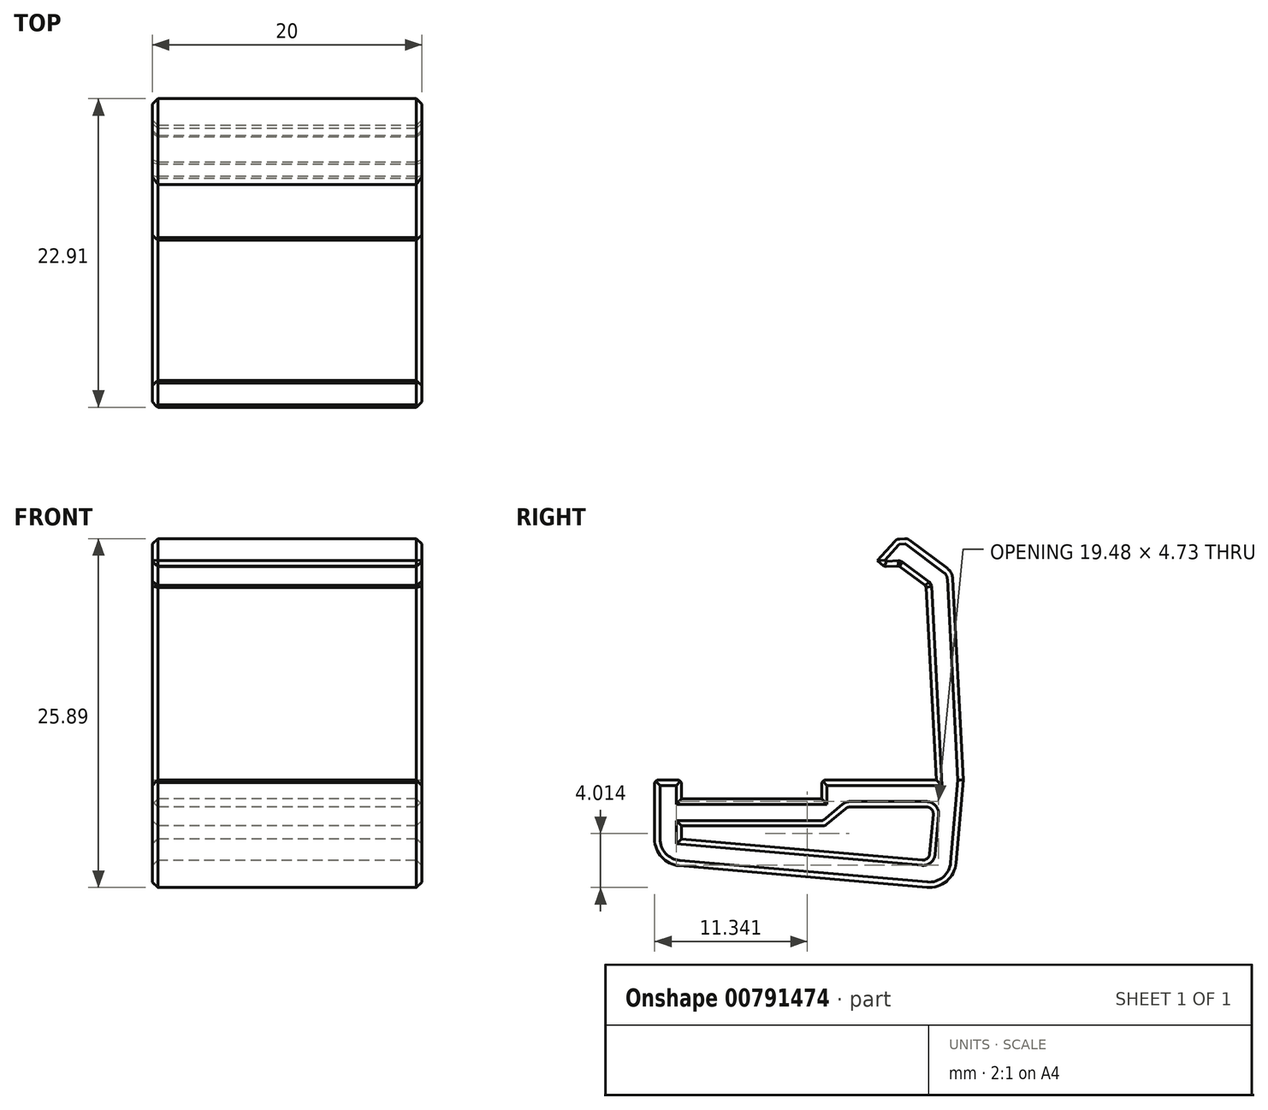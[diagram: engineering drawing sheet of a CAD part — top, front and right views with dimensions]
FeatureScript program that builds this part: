
annotation { "Feature Type Name" : "Feature", "Feature Type Description" : "" }
export const myFeature = defineFeature(function(context is Context, id is Id, definition is map)
    precondition{}
    {
        {
            var Q0;
            Q0=qCreatedBy(makeId("Right.planeOp"),FACE);
            var sketch = newSketch(context, id + "F0", { "sketchPlane" : qUnion([Q0])});
            skLineSegment(sketch, "E0", {"start": v(-30, 0) * mm, "end": v(-18.5, 0) * mm, "construction": true});
            skLineSegment(sketch, "E1", {"start": v(0, 0) * mm, "end": v(-0.82, 15.58) * mm, "construction": true});
            skLineSegment(sketch, "E2", {"start": v(-0.82, 15.58) * mm, "end": v(-8.8, 15.16) * mm, "construction": true});
            skLineSegment(sketch, "E3", {"start": v(-8.5, 0) * mm, "end": v(-8.5, -1.4) * mm, "construction": true});
            skLineSegment(sketch, "E4", {"start": v(-8.5, -1.4) * mm, "end": v(-18.5, -1.4) * mm, "construction": true});
            skLineSegment(sketch, "E5", {"start": v(-18.5, -1.4) * mm, "end": v(-18.5, 0) * mm, "construction": true});
            skLineSegment(sketch, "E6.trimOffspring", {"start": v(-8.5, 0) * mm, "end": v(0, 0) * mm, "construction": true});
            skLineSegment(sketch, "E7.0", {"start": v(-0.63, 15.79) * mm, "end": v(-8.82, 15.36) * mm});
            skLineSegment(sketch, "E7.1", {"start": v(0.21, -0.2) * mm, "end": v(-0.63, 15.79) * mm});
            skLineSegment(sketch, "E7.2", {"start": v(-8.3, -0.2) * mm, "end": v(0.21, -0.2) * mm});
            skLineSegment(sketch, "E7.3", {"start": v(-57.7, -0.2) * mm, "end": v(-18.7, -0.2) * mm});
            skLineSegment(sketch, "E7.4", {"start": v(-18.7, -1.6) * mm, "end": v(-18.7, -0.2) * mm});
            skLineSegment(sketch, "E7.5", {"start": v(-8.3, -1.6) * mm, "end": v(-18.7, -1.6) * mm});
            skLineSegment(sketch, "E7.6", {"start": v(-8.3, -0.2) * mm, "end": v(-8.3, -1.6) * mm});
            skLineSegment(sketch, "E8", {"start": v(-20.7, -0.2) * mm, "end": v(-20.7, -4.57) * mm});
            skLineSegment(sketch, "E9", {"start": v(2.21, -0.2) * mm, "end": v(1.43, 14.76) * mm});
            skLineSegment(sketch, "E10", {"start": v(-2.12, 17.71) * mm, "end": v(-2.53, 17.7) * mm});
            skLineSegment(sketch, "E11", {"start": v(-4.15, 16.1) * mm, "end": v(-4.13, 15.6) * mm, "construction": true});
            skLineSegment(sketch, "E12", {"start": v(2.21, -0.2) * mm, "end": v(1.68, -6.35) * mm});
            skLineSegment(sketch, "E13", {"start": v(-0.5, -8.17) * mm, "end": v(-18.87, -6.56) * mm});
            skPoint(sketch, "E14.visualSharp", {"position": v(1.27, 17.9) * mm});
            skLineSegment(sketch, "E15", {"start": v(-2.62, 15.48) * mm, "end": v(-0.74, 14.08) * mm, "construction": true});
            skLineSegment(sketch, "E16", {"start": v(-2.55, 15.69) * mm, "end": v(-0.54, 14.18) * mm});
            skPoint(sketch, "E17.visualSharp", {"position": v(1.5, -8.34) * mm});
            skArc(sketch, "E17.filletArc", {"start": v(-0.5, -8.17) * mm, "mid": v(0.97, -7.7) * mm, "end": v(1.68, -6.35) * mm});
            skPoint(sketch, "E18.visualSharp", {"position": v(-20.7, -6.4) * mm});
            skArc(sketch, "E18.filletArc", {"start": v(-20.7, -4.57) * mm, "mid": v(-20.17, -5.92) * mm, "end": v(-18.87, -6.56) * mm});
            skLineSegment(sketch, "E19", {"start": v(-4.15, 16.1) * mm, "end": v(-2.87, 17.53) * mm});
            skPoint(sketch, "E20.visualSharp", {"position": v(-2.73, 17.68) * mm});
            skArc(sketch, "E20.filletArc", {"start": v(-2.53, 17.7) * mm, "mid": v(-2.72, 17.64) * mm, "end": v(-2.87, 17.53) * mm});
            skLineSegment(sketch, "E21", {"start": v(-18.7, -3.6) * mm, "end": v(-18.7, -4.57) * mm});
            skLineSegment(sketch, "E22", {"start": v(-18.7, -4.57) * mm, "end": v(-0.32, -6.18) * mm});
            skLineSegment(sketch, "E23", {"start": v(-0.32, -6.18) * mm, "end": v(0.03, -2.2) * mm});
            skLineSegment(sketch, "E24", {"start": v(-18.7, -3.6) * mm, "end": v(-8.04, -3.6) * mm});
            skLineSegment(sketch, "E25", {"start": v(-8.04, -3.6) * mm, "end": v(-6.37, -2.2) * mm});
            skLineSegment(sketch, "E26", {"start": v(-6.37, -2.2) * mm, "end": v(0.03, -2.2) * mm});
            skLineSegment(sketch, "E27", {"start": v(-8.3, -1.6) * mm, "end": v(-8.04, -3.6) * mm, "construction": true});
            skLineSegment(sketch, "E28", {"start": v(-8.3, -1.6) * mm, "end": v(-6.37, -2.2) * mm, "construction": true});
            skLineSegment(sketch, "E29", {"start": v(-1.8, 17.61) * mm, "end": v(1.03, 15.5) * mm});
            skPoint(sketch, "E30.visualSharp", {"position": v(-1.94, 17.72) * mm});
            skArc(sketch, "E30.filletArc", {"start": v(-1.8, 17.61) * mm, "mid": v(-1.95, 17.7) * mm, "end": v(-2.12, 17.71) * mm});
            skPoint(sketch, "E31.visualSharp", {"position": v(1.4, 15.22) * mm});
            skArc(sketch, "E31.filletArc", {"start": v(1.43, 14.76) * mm, "mid": v(1.31, 15.17) * mm, "end": v(1.03, 15.5) * mm});
            skLineSegment(sketch, "E32", {"start": v(-4.15, 16.1) * mm, "end": v(-3.63, 15.63) * mm});
            skSolve(sketch);
        }
        {
            var Q0;
            {var subQ13=sQuery(id+"F0.wireOp",EDGE,"E7.4");Q0=makeQuery(id+"F0.imprint","IMPRINT",FACE,{"disambiguationData":[TD([[makeQuery(id+"F0.imprint","IMPRINT",EDGE,{"derivedFrom":subQ13}),1.0]])]});}
            var Q1;
            {var subQ3=sQuery(id+"F0.wireOp",EDGE,"E16");Q1=makeQuery(id+"F0.imprint","IMPRINT",FACE,{"disambiguationData":[TD([[makeQuery(id+"F0.imprint","IMPRINT",EDGE,{"derivedFrom":subQ3}),1.0]])]});}
            extrude(context, id + "F1", {"entities" : qUnion([Q0, Q1]), "endBound" : BoundingType.SYMMETRIC, "depth" : 20 * mm, "offsetDistance" : 25 * mm});
        }
        {
            var Q0;
            Q0=makeQuery(id+"F1.opExtrude","SWEPT_EDGE",EDGE,{"disambiguationData":[OSD([sQuery(id+"F0.wireOp",EDGE,"E7.3"),sQuery(id+"F0.wireOp",EDGE,"E8")])]});
            var Q1;
            Q1=makeQuery(id+"F1.opExtrude","SWEPT_EDGE",EDGE,{"disambiguationData":[OSD([sQuery(id+"F0.wireOp",EDGE,"E7.3"),sQuery(id+"F0.wireOp",EDGE,"E7.4")])]});
            var Q2;
            Q2=makeQuery(id+"F1.opExtrude","SWEPT_EDGE",EDGE,{"disambiguationData":[OSD([sQuery(id+"F0.wireOp",EDGE,"E7.2"),sQuery(id+"F0.wireOp",EDGE,"E7.6")])]});
            var Q3;
            Q3=makeQuery(id+"F1.opExtrude","SWEPT_EDGE",EDGE,{"disambiguationData":[OSD([sQuery(id+"F0.wireOp",EDGE,"E7.1"),sQuery(id+"F0.wireOp",EDGE,"E16")])]});
            var Q4;
            Q4=makeQuery(id+"F1.opExtrude","SWEPT_EDGE",EDGE,{"disambiguationData":[OSD([sQuery(id+"F0.wireOp",EDGE,"E7.0"),sQuery(id+"F0.wireOp",EDGE,"E16")])]});
            var Q5;
            Q5=makeQuery(id+"F1.opExtrude","SWEPT_EDGE",EDGE,{"disambiguationData":[OSD([sQuery(id+"F0.wireOp",EDGE,"E7.0"),sQuery(id+"F0.wireOp",EDGE,"E11")])]});
            chamfer(context, id + "F2", {"entities" : qUnion([Q0, Q1, Q2, Q3, Q4, Q5]), "width" : 0.2 * mm, "tangentPropagation" : true});
        }
        {
            var Q0;
            Q0=makeQuery(id+"F1.opExtrude","SWEPT_EDGE",EDGE,{"disambiguationData":[OSD([sQuery(id+"F0.wireOp",EDGE,"E22"),sQuery(id+"F0.wireOp",EDGE,"E23")])]});
            var Q1;
            Q1=makeQuery(id+"F1.opExtrude","SWEPT_EDGE",EDGE,{"disambiguationData":[OSD([sQuery(id+"F0.wireOp",EDGE,"E23"),sQuery(id+"F0.wireOp",EDGE,"E26")])]});
            var Q2;
            Q2=makeQuery(id+"F1.opExtrude","SWEPT_EDGE",EDGE,{"disambiguationData":[OSD([sQuery(id+"F0.wireOp",EDGE,"E25"),sQuery(id+"F0.wireOp",EDGE,"E26")])]});
            var Q3;
            Q3=makeQuery(id+"F1.opExtrude","SWEPT_EDGE",EDGE,{"disambiguationData":[OSD([sQuery(id+"F0.wireOp",EDGE,"E24"),sQuery(id+"F0.wireOp",EDGE,"E25")])]});
            fillet(context, id + "F3", {"entities" : qUnion([Q0, Q1, Q2, Q3]), "radius" : .5 * mm, "tangentPropagation" : true, "allowEdgeOverflow" : false});
        }
        {
            var Q0;
            Q0=makeQuery(id+"F1.opExtrude","CAP_FACE",FACE,{"disambiguationData":[OSD([sQuery(id+"F0.wireOp",EDGE,"E7.0"),sQuery(id+"F0.wireOp",EDGE,"E7.1"),sQuery(id+"F0.wireOp",EDGE,"E7.2"),sQuery(id+"F0.wireOp",EDGE,"E7.3"),sQuery(id+"F0.wireOp",EDGE,"E7.4"),sQuery(id+"F0.wireOp",EDGE,"E7.5"),sQuery(id+"F0.wireOp",EDGE,"E7.6"),sQuery(id+"F0.wireOp",EDGE,"E8"),sQuery(id+"F0.wireOp",EDGE,"E9"),sQuery(id+"F0.wireOp",EDGE,"E10"),sQuery(id+"F0.wireOp",EDGE,"E11"),sQuery(id+"F0.wireOp",EDGE,"E12"),sQuery(id+"F0.wireOp",EDGE,"E13"),sQuery(id+"F0.wireOp",EDGE,"E14.filletArc"),sQuery(id+"F0.wireOp",EDGE,"E16"),sQuery(id+"F0.wireOp",EDGE,"E17.filletArc"),sQuery(id+"F0.wireOp",EDGE,"E18.filletArc"),sQuery(id+"F0.wireOp",EDGE,"E19"),sQuery(id+"F0.wireOp",EDGE,"E20.filletArc"),sQuery(id+"F0.wireOp",EDGE,"E21"),sQuery(id+"F0.wireOp",EDGE,"E22"),sQuery(id+"F0.wireOp",EDGE,"E23"),sQuery(id+"F0.wireOp",EDGE,"E24"),sQuery(id+"F0.wireOp",EDGE,"E25"),sQuery(id+"F0.wireOp",EDGE,"E26")])],"isStart":false});
            var Q1;
            Q1=makeQuery(id+"F1.opExtrude","CAP_FACE",FACE,{"disambiguationData":[OSD([sQuery(id+"F0.wireOp",EDGE,"E7.0"),sQuery(id+"F0.wireOp",EDGE,"E7.1"),sQuery(id+"F0.wireOp",EDGE,"E7.2"),sQuery(id+"F0.wireOp",EDGE,"E7.3"),sQuery(id+"F0.wireOp",EDGE,"E7.4"),sQuery(id+"F0.wireOp",EDGE,"E7.5"),sQuery(id+"F0.wireOp",EDGE,"E7.6"),sQuery(id+"F0.wireOp",EDGE,"E8"),sQuery(id+"F0.wireOp",EDGE,"E9"),sQuery(id+"F0.wireOp",EDGE,"E10"),sQuery(id+"F0.wireOp",EDGE,"E11"),sQuery(id+"F0.wireOp",EDGE,"E12"),sQuery(id+"F0.wireOp",EDGE,"E13"),sQuery(id+"F0.wireOp",EDGE,"E16"),sQuery(id+"F0.wireOp",EDGE,"E17.filletArc"),sQuery(id+"F0.wireOp",EDGE,"E18.filletArc"),sQuery(id+"F0.wireOp",EDGE,"E19"),sQuery(id+"F0.wireOp",EDGE,"E20.filletArc"),sQuery(id+"F0.wireOp",EDGE,"E21"),sQuery(id+"F0.wireOp",EDGE,"E22"),sQuery(id+"F0.wireOp",EDGE,"E23"),sQuery(id+"F0.wireOp",EDGE,"E24"),sQuery(id+"F0.wireOp",EDGE,"E25"),sQuery(id+"F0.wireOp",EDGE,"E26"),sQuery(id+"F0.wireOp",EDGE,"E29"),sQuery(id+"F0.wireOp",EDGE,"E30.filletArc"),sQuery(id+"F0.wireOp",EDGE,"E31.filletArc")])],"isStart":true});
            chamfer(context, id + "F4", {"entities" : qUnion([Q0, Q1]), "width" : 0.4 * mm, "tangentPropagation" : true});
        }
    });
